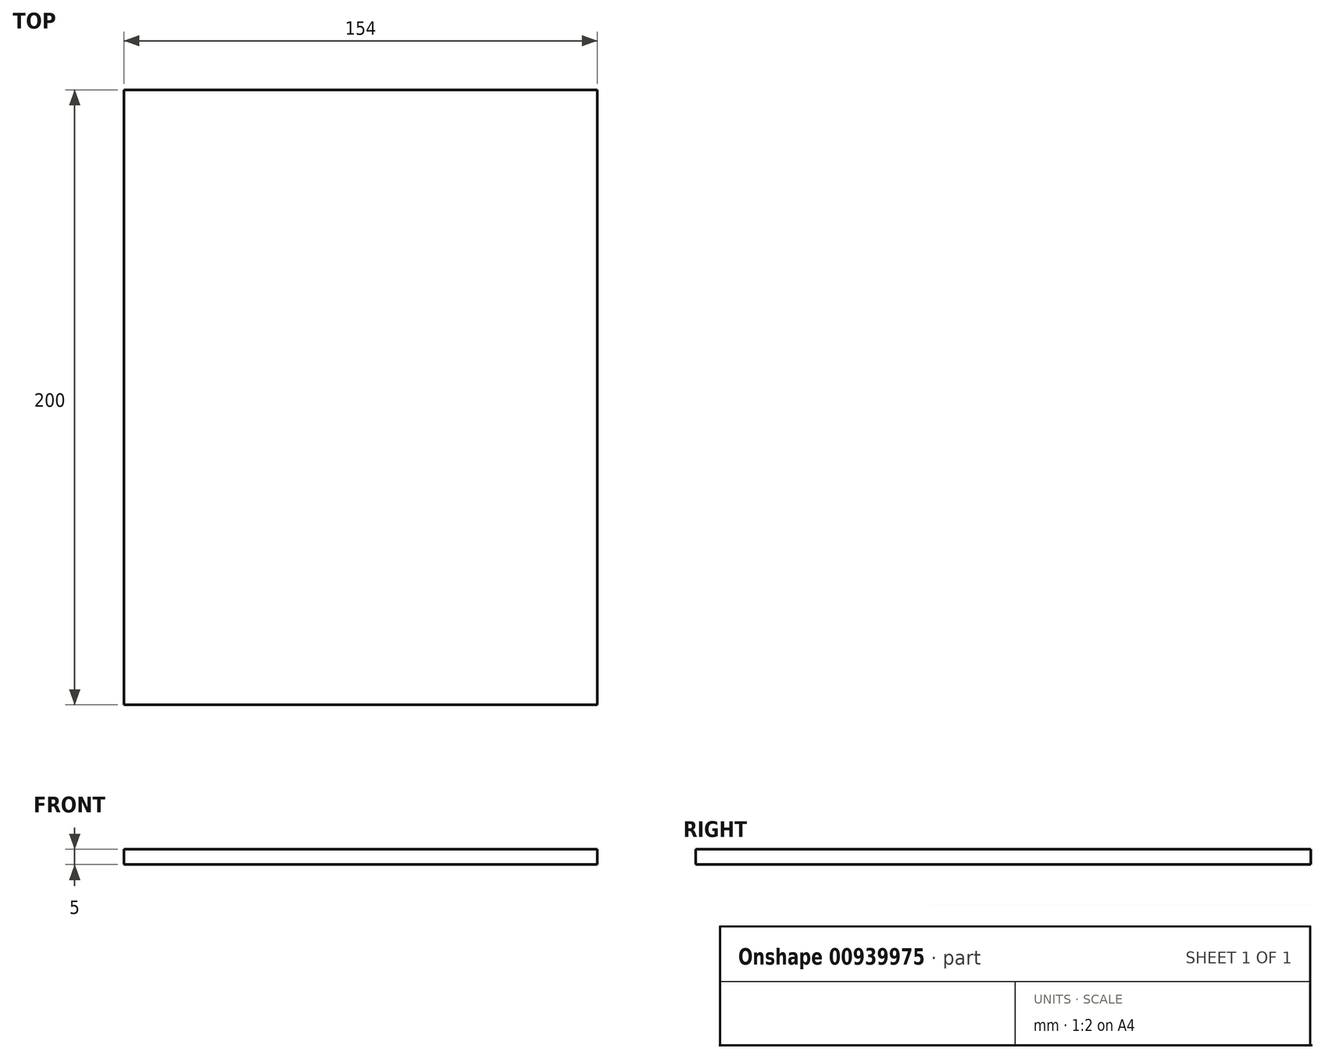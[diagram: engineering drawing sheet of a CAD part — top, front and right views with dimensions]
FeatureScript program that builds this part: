
annotation { "Feature Type Name" : "Feature", "Feature Type Description" : "" }
export const myFeature = defineFeature(function(context is Context, id is Id, definition is map)
    precondition{}
    {
        {
            var Q0;
            Q0=qCreatedBy(makeId("Top.planeOp"),FACE);
            var sketch = newSketch(context, id + "F0", { "sketchPlane" : qUnion([Q0])});
            skLineSegment(sketch, "E0.bottom", {"start": v(0, 0) * mm, "end": v(154, 0) * mm});
            skLineSegment(sketch, "E0.top", {"start": v(0, 200) * mm, "end": v(154, 200) * mm});
            skLineSegment(sketch, "E0.left", {"start": v(0, 0) * mm, "end": v(0, 200) * mm});
            skLineSegment(sketch, "E0.right", {"start": v(154, 0) * mm, "end": v(154, 200) * mm});
            skSolve(sketch);
        }
        {
            var Q0;
            Q0=makeQuery(id+"F0.imprint","IMPRINT",FACE,{"disambiguationData":[TD([[makeQuery(id+"F0.imprint","IMPRINT",EDGE,{"derivedFrom":sQuery(id+"F0.wireOp",EDGE,"E0.bottom")}),1.0]])]});
            extrude(context, id + "F1", {"entities" : qUnion([Q0]), "depth" : 5 * mm, "offsetDistance" : 25 * mm});
        }
    });
